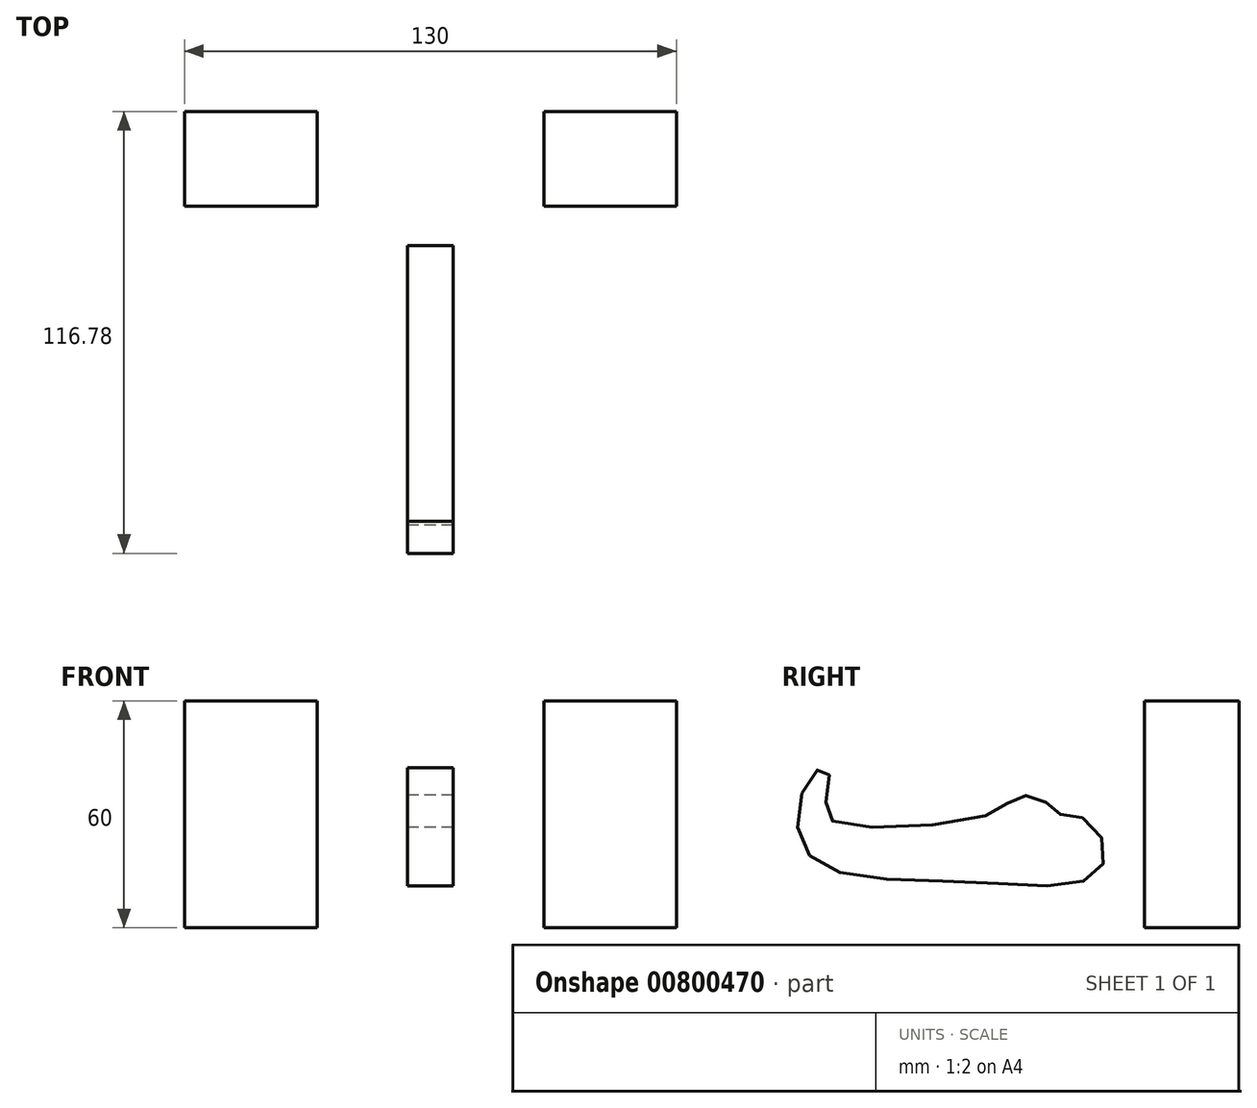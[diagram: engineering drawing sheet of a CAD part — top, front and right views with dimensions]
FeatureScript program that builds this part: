
annotation { "Feature Type Name" : "Feature", "Feature Type Description" : "" }
export const myFeature = defineFeature(function(context is Context, id is Id, definition is map)
    precondition{}
    {
        {
            var Q0;
            Q0=qCreatedBy(makeId("Front.planeOp"),FACE);
            var sketch = newSketch(context, id + "F0", { "sketchPlane" : qUnion([Q0])});
            skLineSegment(sketch, "E0.bottom", {"start": v(-30, 0) * mm, "end": v(-65, 0) * mm});
            skLineSegment(sketch, "E0.top", {"start": v(-30, 60) * mm, "end": v(-65, 60) * mm});
            skLineSegment(sketch, "E0.left", {"start": v(-30, 0) * mm, "end": v(-30, 60) * mm});
            skLineSegment(sketch, "E0.right", {"start": v(-65, 0) * mm, "end": v(-65, 60) * mm});
            skLineSegment(sketch, "E1.MirrorCS", {"start": v(30, 0) * mm, "end": v(30, 60) * mm});
            skLineSegment(sketch, "E2.MirrorCS", {"start": v(30, 60) * mm, "end": v(65, 60) * mm});
            skLineSegment(sketch, "E3.MirrorCS", {"start": v(65, 0) * mm, "end": v(65, 60) * mm});
            skLineSegment(sketch, "E4.MirrorCS", {"start": v(30, 0) * mm, "end": v(65, 0) * mm});
            skSolve(sketch);
        }
        {
            var Q0;
            Q0=makeQuery(id+"F0.imprint","IMPRINT",FACE,{"disambiguationData":[TD([[makeQuery(id+"F0.imprint","IMPRINT",EDGE,{"derivedFrom":sQuery(id+"F0.wireOp",EDGE,"E0.bottom")}),-1.0]])]});
            var Q1;
            Q1=makeQuery(id+"F0.imprint","IMPRINT",FACE,{"disambiguationData":[TD([[makeQuery(id+"F0.imprint","IMPRINT",EDGE,{"derivedFrom":sQuery(id+"F0.wireOp",EDGE,"E1.MirrorCS")}),-1.0]])]});
            extrude(context, id + "F1", {"entities" : qUnion([Q0, Q1]), "endBound" : BoundingType.SYMMETRIC, "depth" : 25 * mm, "offsetDistance" : 25 * mm});
        }
        {
            var Q0;
            Q0=qCreatedBy(makeId("Right.planeOp"),FACE);
            var sketch = newSketch(context, id + "F2", { "sketchPlane" : qUnion([Q0])});
            skFitSpline(sketch, "E5", {"points": [v(-28.88, 29.08) * mm, v(-35.88, 30.28) * mm, v(-39.87, 34.28) * mm, v(-47.27, 34.08) * mm, v(-52.47, 30.28) * mm, v(-93.04, 27.48) * mm, v(-96.84, 32.08) * mm, v(-96.24, 41.67) * mm, v(-99.84, 41.07) * mm, v(-104.23, 26.88) * mm, v(-96.24, 15.7) * mm, v(-57.46, 12.1) * mm, v(-28.08, 12.5) * mm, v(-22.89, 20.09) * mm, v(-28.88, 29.08) * mm]});
            skSolve(sketch);
        }
        {
            var Q0;
            Q0 = qSketchRegion(id + "F2", true);
            extrude(context, id + "F3", {"entities" : qUnion([Q0]), "endBound" : BoundingType.SYMMETRIC, "depth" : 12 * mm, "offsetDistance" : 25 * mm});
        }
    });
